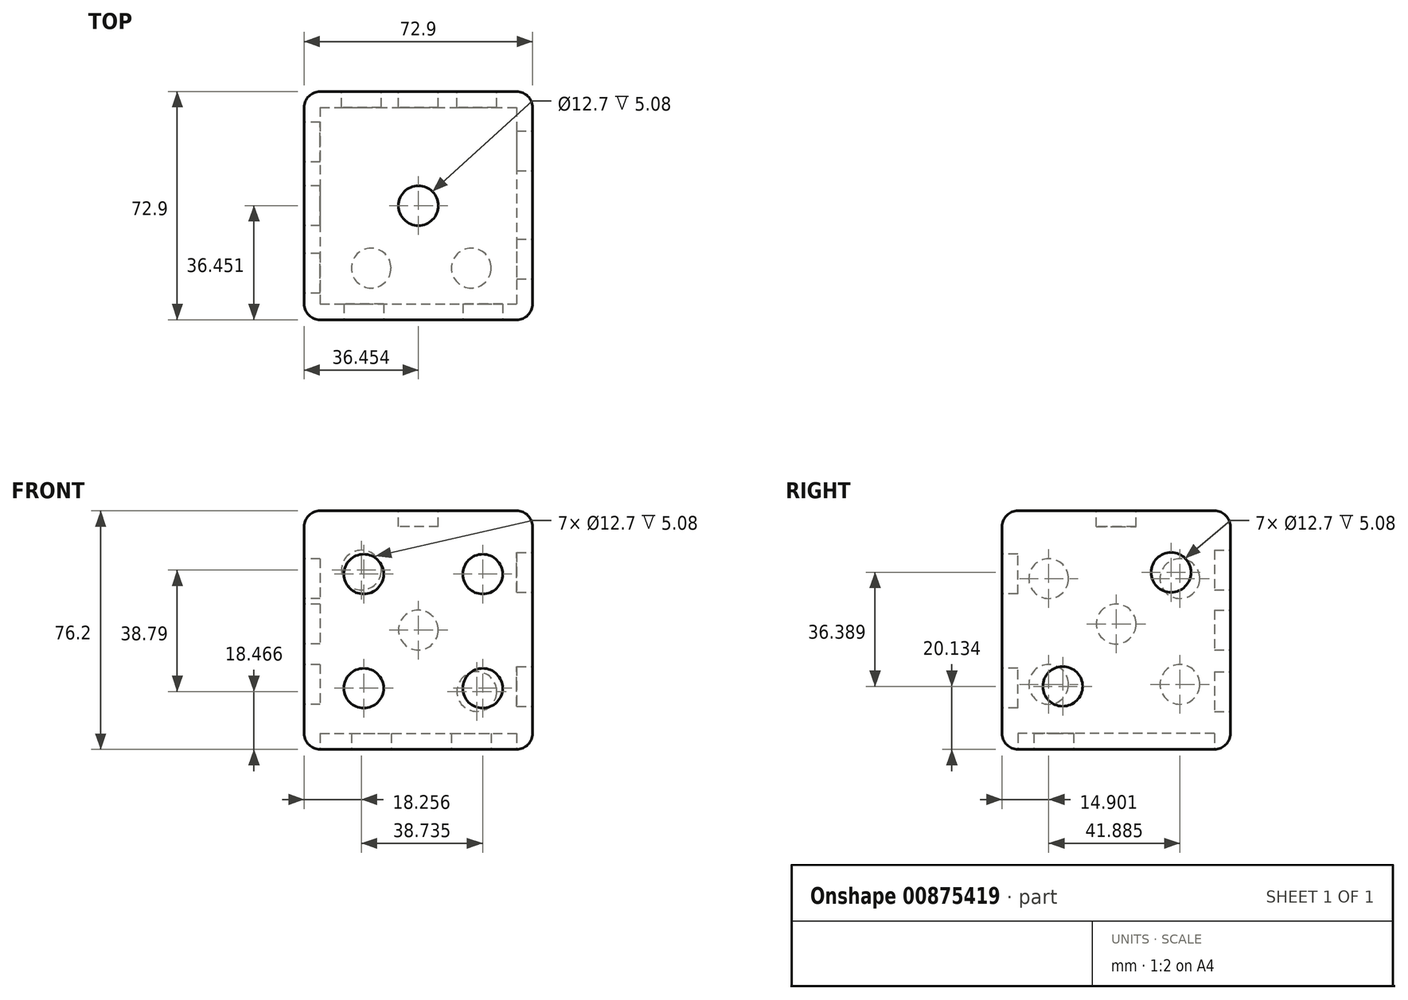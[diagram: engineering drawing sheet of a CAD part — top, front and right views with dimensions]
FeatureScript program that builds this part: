
annotation { "Feature Type Name" : "Feature", "Feature Type Description" : "" }
export const myFeature = defineFeature(function(context is Context, id is Id, definition is map)
    precondition{}
    {
        {
            var Q0;
            Q0=qCreatedBy(makeId("Top.planeOp"),FACE);
            var sketch = newSketch(context, id + "F0", { "sketchPlane" : qUnion([Q0])});
            skLineSegment(sketch, "E0.bottom", {"start": v(-93.39, 58.05) * mm, "end": v(-20.49, 58.05) * mm});
            skLineSegment(sketch, "E0.top", {"start": v(-93.39, -14.85) * mm, "end": v(-20.49, -14.85) * mm});
            skLineSegment(sketch, "E0.left", {"start": v(-93.39, 58.05) * mm, "end": v(-93.39, -14.85) * mm});
            skLineSegment(sketch, "E0.right", {"start": v(-20.49, 58.05) * mm, "end": v(-20.49, -14.85) * mm});
            skSolve(sketch);
        }
        {
            var Q0;
            Q0=makeQuery(id+"F0.imprint","IMPRINT",FACE,{"disambiguationData":[TD([[makeQuery(id+"F0.imprint","IMPRINT",EDGE,{"derivedFrom":sQuery(id+"F0.wireOp",EDGE,"E0.bottom")}),-1.0]])]});
            extrude(context, id + "F1", {"entities" : qUnion([Q0]), "depth" : 76.2 * mm, "offsetDistance" : 25.4 * mm});
        }
        {
            var Q0;
            Q0=makeQuery(id+"F1.opExtrude","CAP_EDGE",EDGE,{"disambiguationData":[OSD([sQuery(id+"F0.wireOp",EDGE,"E0.right")])],"isStart":false});
            var Q1;
            Q1=makeQuery(id+"F1.opExtrude","SWEPT_EDGE",EDGE,{"disambiguationData":[OSD([sQuery(id+"F0.wireOp",EDGE,"E0.bottom"),sQuery(id+"F0.wireOp",EDGE,"E0.left")])]});
            var Q2;
            Q2=makeQuery(id+"F1.opExtrude","CAP_EDGE",EDGE,{"disambiguationData":[OSD([sQuery(id+"F0.wireOp",EDGE,"E0.bottom")])],"isStart":true});
            var Q3;
            Q3=makeQuery(id+"F1.opExtrude","SWEPT_EDGE",EDGE,{"disambiguationData":[OSD([sQuery(id+"F0.wireOp",EDGE,"E0.bottom"),sQuery(id+"F0.wireOp",EDGE,"E0.right")])]});
            var Q4;
            Q4=makeQuery(id+"F1.opExtrude","CAP_EDGE",EDGE,{"disambiguationData":[OSD([sQuery(id+"F0.wireOp",EDGE,"E0.right")])],"isStart":true});
            var Q5;
            Q5=makeQuery(id+"F1.opExtrude","CAP_EDGE",EDGE,{"disambiguationData":[OSD([sQuery(id+"F0.wireOp",EDGE,"E0.bottom")])],"isStart":false});
            var Q6;
            Q6=makeQuery(id+"F1.opExtrude","SWEPT_EDGE",EDGE,{"disambiguationData":[OSD([sQuery(id+"F0.wireOp",EDGE,"E0.top"),sQuery(id+"F0.wireOp",EDGE,"E0.right")])]});
            var Q7;
            Q7=makeQuery(id+"F1.opExtrude","CAP_EDGE",EDGE,{"disambiguationData":[OSD([sQuery(id+"F0.wireOp",EDGE,"E0.left")])],"isStart":true});
            var Q8;
            Q8=makeQuery(id+"F1.opExtrude","CAP_EDGE",EDGE,{"disambiguationData":[OSD([sQuery(id+"F0.wireOp",EDGE,"E0.top")])],"isStart":true});
            var Q9;
            Q9=makeQuery(id+"F1.opExtrude","CAP_EDGE",EDGE,{"disambiguationData":[OSD([sQuery(id+"F0.wireOp",EDGE,"E0.top")])],"isStart":false});
            var Q10;
            Q10=makeQuery(id+"F1.opExtrude","SWEPT_EDGE",EDGE,{"disambiguationData":[OSD([sQuery(id+"F0.wireOp",EDGE,"E0.top"),sQuery(id+"F0.wireOp",EDGE,"E0.left")])]});
            var Q11;
            Q11=makeQuery(id+"F1.opExtrude","CAP_EDGE",EDGE,{"disambiguationData":[OSD([sQuery(id+"F0.wireOp",EDGE,"E0.left")])],"isStart":false});
            fillet(context, id + "F2", {"entities" : qUnion([Q0, Q1, Q2, Q3, Q4, Q5, Q6, Q7, Q8, Q9, Q10, Q11]), "radius" : 5.08 * mm, "tangentPropagation" : true, "allowEdgeOverflow" : false});
        }
        {
            var Q0;
            Q0=makeQuery(id+"F1.opExtrude","CAP_FACE",FACE,{"disambiguationData":[OSD([sQuery(id+"F0.wireOp",EDGE,"E0.bottom"),sQuery(id+"F0.wireOp",EDGE,"E0.top"),sQuery(id+"F0.wireOp",EDGE,"E0.left"),sQuery(id+"F0.wireOp",EDGE,"E0.right")])],"isStart":false});
            var sketch = newSketch(context, id + "F3", { "sketchPlane" : qUnion([Q0])});
            skLineSegment(sketch, "E1.0.0", {"start": v(-88.3, -9.77) * mm, "end": v(-25.57, -9.77) * mm});
            skLineSegment(sketch, "E1.0.1", {"start": v(-25.57, -9.77) * mm, "end": v(-25.57, 52.97) * mm});
            skLineSegment(sketch, "E1.0.2", {"start": v(-25.57, 52.97) * mm, "end": v(-88.3, 52.97) * mm});
            skLineSegment(sketch, "E1.0.3", {"start": v(-88.3, 52.97) * mm, "end": v(-88.3, -9.77) * mm});
            skLineSegment(sketch, "E2", {"start": v(-56.94, 52.97) * mm, "end": v(-56.94, -9.77) * mm, "construction": true});
            skLineSegment(sketch, "E3", {"start": v(-88.3, 21.6) * mm, "end": v(-25.57, 21.6) * mm, "construction": true});
            skCircle(sketch, "E4", {"center": v(-56.94, 21.6) * mm, "radius": 6.35 * mm});
            skSolve(sketch);
        }
        {
            var Q0;
            Q0=makeQuery(id+"F3.imprint","IMPRINT",FACE,{"disambiguationData":[TD([[makeQuery(id+"F3.imprint","IMPRINT",EDGE,{"derivedFrom":sQuery(id+"F3.wireOp",EDGE,"E4")}),1.0]])]});
            extrude(context, id + "F4", {"entities" : qUnion([Q0]), "operationType" : NewBodyOperationType.REMOVE, "oppositeDirection" : true, "depth" : 5.08 * mm, "offsetDistance" : 25.4 * mm});
        }
        {
            var Q0;
            Q0=makeQuery(id+"F1.opExtrude","CAP_FACE",FACE,{"disambiguationData":[OSD([sQuery(id+"F0.wireOp",EDGE,"E0.bottom"),sQuery(id+"F0.wireOp",EDGE,"E0.top"),sQuery(id+"F0.wireOp",EDGE,"E0.left"),sQuery(id+"F0.wireOp",EDGE,"E0.right")])],"isStart":true});
            var sketch = newSketch(context, id + "F5", { "sketchPlane" : qUnion([Q0])});
            skLineSegment(sketch, "E5.0.0", {"start": v(-88.3, -52.97) * mm, "end": v(-25.57, -52.97) * mm});
            skLineSegment(sketch, "E5.0.1", {"start": v(-25.57, -52.97) * mm, "end": v(-25.57, 9.77) * mm});
            skLineSegment(sketch, "E5.0.2", {"start": v(-25.57, 9.77) * mm, "end": v(-88.3, 9.77) * mm});
            skLineSegment(sketch, "E5.0.3", {"start": v(-88.3, 9.77) * mm, "end": v(-88.3, -52.97) * mm});
            skLineSegment(sketch, "E6", {"start": v(-72, 9.77) * mm, "end": v(-72, -52.97) * mm});
            skLineSegment(sketch, "E7", {"start": v(-40.03, 9.77) * mm, "end": v(-40.03, -52.97) * mm});
            skCircle(sketch, "E8", {"center": v(-72, -1.66) * mm, "radius": 6.35 * mm});
            skCircle(sketch, "E9", {"center": v(-72, -21.6) * mm, "radius": 6.35 * mm});
            skCircle(sketch, "E10", {"center": v(-72, -41.54) * mm, "radius": 6.35 * mm});
            skCircle(sketch, "E11", {"center": v(-40.03, -1.66) * mm, "radius": 6.35 * mm});
            skCircle(sketch, "E12", {"center": v(-40.03, -21.6) * mm, "radius": 6.35 * mm});
            skCircle(sketch, "E13", {"center": v(-40.03, -41.54) * mm, "radius": 6.35 * mm});
            skSolve(sketch);
        }
        {
            var Q0;
            {var subQ0=sQuery(id+"F5.wireOp",EDGE,"E8");var subQ1=sQuery(id+"F5.wireOp",EDGE,"E6");var subQ2=makeQuery(id+"F5.imprint","INTERSECT",VERTEX,{"disambiguationData":[OD(0.0)],"derivedFrom":[subQ1,subQ0]});Q0=makeQuery(id+"F5.imprint","IMPRINT",FACE,{"disambiguationData":[TD([[makeQuery(id+"F5.imprint","IMPRINT",EDGE,{"disambiguationData":[TD([[subQ2,-1.0]])],"derivedFrom":subQ1}),-1.0]])]});}
            var Q1;
            {var subQ0=sQuery(id+"F5.wireOp",EDGE,"E8");var subQ1=sQuery(id+"F5.wireOp",EDGE,"E6");var subQ2=makeQuery(id+"F5.imprint","INTERSECT",VERTEX,{"disambiguationData":[OD(0.0)],"derivedFrom":[subQ1,subQ0]});Q1=makeQuery(id+"F5.imprint","IMPRINT",FACE,{"disambiguationData":[TD([[makeQuery(id+"F5.imprint","IMPRINT",EDGE,{"disambiguationData":[TD([[subQ2,-1.0]])],"derivedFrom":subQ1}),1.0]])]});}
            var Q2;
            {var subQ0=sQuery(id+"F5.wireOp",EDGE,"E9");var subQ1=sQuery(id+"F5.wireOp",EDGE,"E6");var subQ2=makeQuery(id+"F5.imprint","INTERSECT",VERTEX,{"disambiguationData":[OD(0.0)],"derivedFrom":[subQ1,subQ0]});Q2=makeQuery(id+"F5.imprint","IMPRINT",FACE,{"disambiguationData":[TD([[makeQuery(id+"F5.imprint","IMPRINT",EDGE,{"disambiguationData":[TD([[subQ2,-1.0]])],"derivedFrom":subQ1}),-1.0]])]});}
            var Q3;
            {var subQ0=sQuery(id+"F5.wireOp",EDGE,"E9");var subQ1=sQuery(id+"F5.wireOp",EDGE,"E6");var subQ2=makeQuery(id+"F5.imprint","INTERSECT",VERTEX,{"disambiguationData":[OD(0.0)],"derivedFrom":[subQ1,subQ0]});Q3=makeQuery(id+"F5.imprint","IMPRINT",FACE,{"disambiguationData":[TD([[makeQuery(id+"F5.imprint","IMPRINT",EDGE,{"disambiguationData":[TD([[subQ2,-1.0]])],"derivedFrom":subQ1}),1.0]])]});}
            var Q4;
            {var subQ0=sQuery(id+"F5.wireOp",EDGE,"E10");var subQ1=sQuery(id+"F5.wireOp",EDGE,"E6");var subQ2=makeQuery(id+"F5.imprint","INTERSECT",VERTEX,{"disambiguationData":[OD(0.0)],"derivedFrom":[subQ1,subQ0]});Q4=makeQuery(id+"F5.imprint","IMPRINT",FACE,{"disambiguationData":[TD([[makeQuery(id+"F5.imprint","IMPRINT",EDGE,{"disambiguationData":[TD([[subQ2,-1.0]])],"derivedFrom":subQ1}),-1.0]])]});}
            var Q5;
            {var subQ0=sQuery(id+"F5.wireOp",EDGE,"E13");var subQ1=sQuery(id+"F5.wireOp",EDGE,"E7");var subQ2=makeQuery(id+"F5.imprint","INTERSECT",VERTEX,{"disambiguationData":[OD(0.0)],"derivedFrom":[subQ1,subQ0]});Q5=makeQuery(id+"F5.imprint","IMPRINT",FACE,{"disambiguationData":[TD([[makeQuery(id+"F5.imprint","IMPRINT",EDGE,{"disambiguationData":[TD([[subQ2,-1.0]])],"derivedFrom":subQ1}),-1.0]])]});}
            var Q6;
            {var subQ0=sQuery(id+"F5.wireOp",EDGE,"E13");var subQ1=sQuery(id+"F5.wireOp",EDGE,"E7");var subQ2=makeQuery(id+"F5.imprint","INTERSECT",VERTEX,{"disambiguationData":[OD(0.0)],"derivedFrom":[subQ1,subQ0]});Q6=makeQuery(id+"F5.imprint","IMPRINT",FACE,{"disambiguationData":[TD([[makeQuery(id+"F5.imprint","IMPRINT",EDGE,{"disambiguationData":[TD([[subQ2,-1.0]])],"derivedFrom":subQ1}),1.0]])]});}
            var Q7;
            {var subQ0=sQuery(id+"F5.wireOp",EDGE,"E12");var subQ1=sQuery(id+"F5.wireOp",EDGE,"E7");var subQ2=makeQuery(id+"F5.imprint","INTERSECT",VERTEX,{"disambiguationData":[OD(0.0)],"derivedFrom":[subQ1,subQ0]});Q7=makeQuery(id+"F5.imprint","IMPRINT",FACE,{"disambiguationData":[TD([[makeQuery(id+"F5.imprint","IMPRINT",EDGE,{"disambiguationData":[TD([[subQ2,-1.0]])],"derivedFrom":subQ1}),-1.0]])]});}
            var Q8;
            {var subQ0=sQuery(id+"F5.wireOp",EDGE,"E12");var subQ1=sQuery(id+"F5.wireOp",EDGE,"E7");var subQ2=makeQuery(id+"F5.imprint","INTERSECT",VERTEX,{"disambiguationData":[OD(0.0)],"derivedFrom":[subQ1,subQ0]});Q8=makeQuery(id+"F5.imprint","IMPRINT",FACE,{"disambiguationData":[TD([[makeQuery(id+"F5.imprint","IMPRINT",EDGE,{"disambiguationData":[TD([[subQ2,-1.0]])],"derivedFrom":subQ1}),1.0]])]});}
            var Q9;
            {var subQ0=sQuery(id+"F5.wireOp",EDGE,"E11");var subQ1=sQuery(id+"F5.wireOp",EDGE,"E7");var subQ2=makeQuery(id+"F5.imprint","INTERSECT",VERTEX,{"disambiguationData":[OD(0.0)],"derivedFrom":[subQ1,subQ0]});Q9=makeQuery(id+"F5.imprint","IMPRINT",FACE,{"disambiguationData":[TD([[makeQuery(id+"F5.imprint","IMPRINT",EDGE,{"disambiguationData":[TD([[subQ2,-1.0]])],"derivedFrom":subQ1}),-1.0]])]});}
            var Q10;
            {var subQ0=sQuery(id+"F5.wireOp",EDGE,"E11");var subQ1=sQuery(id+"F5.wireOp",EDGE,"E7");var subQ2=makeQuery(id+"F5.imprint","INTERSECT",VERTEX,{"disambiguationData":[OD(0.0)],"derivedFrom":[subQ1,subQ0]});Q10=makeQuery(id+"F5.imprint","IMPRINT",FACE,{"disambiguationData":[TD([[makeQuery(id+"F5.imprint","IMPRINT",EDGE,{"disambiguationData":[TD([[subQ2,-1.0]])],"derivedFrom":subQ1}),1.0]])]});}
            var Q11;
            {var subQ0=sQuery(id+"F5.wireOp",EDGE,"E10");var subQ1=sQuery(id+"F5.wireOp",EDGE,"E6");var subQ2=makeQuery(id+"F5.imprint","INTERSECT",VERTEX,{"disambiguationData":[OD(0.0)],"derivedFrom":[subQ1,subQ0]});Q11=makeQuery(id+"F5.imprint","IMPRINT",FACE,{"disambiguationData":[TD([[makeQuery(id+"F5.imprint","IMPRINT",EDGE,{"disambiguationData":[TD([[subQ2,-1.0]])],"derivedFrom":subQ1}),1.0]])]});}
            extrude(context, id + "F6", {"entities" : qUnion([Q0, Q1, Q2, Q3, Q4, Q5, Q6, Q7, Q8, Q9, Q10, Q11]), "operationType" : NewBodyOperationType.REMOVE, "oppositeDirection" : true, "depth" : 5.08 * mm, "offsetDistance" : 25.4 * mm});
        }
        {
            var Q0;
            Q0=makeQuery(id+"F1.opExtrude","SWEPT_FACE",FACE,{"disambiguationData":[OSD([sQuery(id+"F0.wireOp",EDGE,"E0.right")])]});
            var sketch = newSketch(context, id + "F7", { "sketchPlane" : qUnion([Q0])});
            skLineSegment(sketch, "E14", {"start": v(52.97, 71.12) * mm, "end": v(-9.77, 5.08) * mm, "construction": true});
            skCircle(sketch, "E15", {"center": v(39.1, 56.52) * mm, "radius": 6.35 * mm});
            skCircle(sketch, "E16", {"center": v(4.53, 20.13) * mm, "radius": 6.35 * mm});
            skSolve(sketch);
        }
        {
            var Q0;
            Q0=makeQuery(id+"F7.imprint","IMPRINT",FACE,{"disambiguationData":[TD([[makeQuery(id+"F7.imprint","IMPRINT",EDGE,{"derivedFrom":sQuery(id+"F7.wireOp",EDGE,"E15")}),1.0]])]});
            var Q1;
            Q1=makeQuery(id+"F7.imprint","IMPRINT",FACE,{"disambiguationData":[TD([[makeQuery(id+"F7.imprint","IMPRINT",EDGE,{"derivedFrom":sQuery(id+"F7.wireOp",EDGE,"E16")}),1.0]])]});
            extrude(context, id + "F8", {"entities" : qUnion([Q0, Q1]), "operationType" : NewBodyOperationType.REMOVE, "oppositeDirection" : true, "depth" : 5.08 * mm, "offsetDistance" : 25.4 * mm});
        }
        {
            var Q0;
            Q0=makeQuery(id+"F1.opExtrude","SWEPT_FACE",FACE,{"disambiguationData":[OSD([sQuery(id+"F0.wireOp",EDGE,"E0.bottom")])]});
            var sketch = newSketch(context, id + "F9", { "sketchPlane" : qUnion([Q0])});
            skLineSegment(sketch, "E17", {"start": v(25.57, 5.08) * mm, "end": v(88.3, 71.12) * mm, "construction": true});
            skCircle(sketch, "E18", {"center": v(56.94, 38.1) * mm, "radius": 6.35 * mm});
            skCircle(sketch, "E19", {"center": v(38.28, 18.47) * mm, "radius": 6.35 * mm});
            skCircle(sketch, "E20", {"center": v(75.13, 57.26) * mm, "radius": 6.35 * mm});
            skSolve(sketch);
        }
        {
            var Q0;
            Q0=makeQuery(id+"F9.imprint","IMPRINT",FACE,{"disambiguationData":[TD([[makeQuery(id+"F9.imprint","IMPRINT",EDGE,{"derivedFrom":sQuery(id+"F9.wireOp",EDGE,"E20")}),1.0]])]});
            var Q1;
            Q1=makeQuery(id+"F9.imprint","IMPRINT",FACE,{"disambiguationData":[TD([[makeQuery(id+"F9.imprint","IMPRINT",EDGE,{"derivedFrom":sQuery(id+"F9.wireOp",EDGE,"E18")}),1.0]])]});
            var Q2;
            Q2=makeQuery(id+"F9.imprint","IMPRINT",FACE,{"disambiguationData":[TD([[makeQuery(id+"F9.imprint","IMPRINT",EDGE,{"derivedFrom":sQuery(id+"F9.wireOp",EDGE,"E19")}),1.0]])]});
            extrude(context, id + "F10", {"entities" : qUnion([Q0, Q1, Q2]), "operationType" : NewBodyOperationType.REMOVE, "oppositeDirection" : true, "depth" : 5.08 * mm, "offsetDistance" : 25.4 * mm});
        }
        {
            var Q0;
            Q0=makeQuery(id+"F1.opExtrude","SWEPT_FACE",FACE,{"disambiguationData":[OSD([sQuery(id+"F0.wireOp",EDGE,"E0.top")])]});
            var sketch = newSketch(context, id + "F11", { "sketchPlane" : qUnion([Q0])});
            skLineSegment(sketch, "E21", {"start": v(-74.36, 71.12) * mm, "end": v(-74.36, 5.08) * mm, "construction": true});
            skLineSegment(sketch, "E22", {"start": v(-36.4, 71.12) * mm, "end": v(-36.4, 5.08) * mm, "construction": true});
            skCircle(sketch, "E23", {"center": v(-74.36, 55.97) * mm, "radius": 6.35 * mm});
            skCircle(sketch, "E24", {"center": v(-74.36, 19.52) * mm, "radius": 6.35 * mm});
            skCircle(sketch, "E25", {"center": v(-36.4, 55.97) * mm, "radius": 6.35 * mm});
            skCircle(sketch, "E26", {"center": v(-36.4, 19.52) * mm, "radius": 6.35 * mm});
            skSolve(sketch);
        }
        {
            var Q0;
            Q0=makeQuery(id+"F11.imprint","IMPRINT",FACE,{"disambiguationData":[TD([[makeQuery(id+"F11.imprint","IMPRINT",EDGE,{"derivedFrom":sQuery(id+"F11.wireOp",EDGE,"E23")}),1.0]])]});
            var Q1;
            Q1=makeQuery(id+"F11.imprint","IMPRINT",FACE,{"disambiguationData":[TD([[makeQuery(id+"F11.imprint","IMPRINT",EDGE,{"derivedFrom":sQuery(id+"F11.wireOp",EDGE,"E25")}),1.0]])]});
            var Q2;
            Q2=makeQuery(id+"F11.imprint","IMPRINT",FACE,{"disambiguationData":[TD([[makeQuery(id+"F11.imprint","IMPRINT",EDGE,{"derivedFrom":sQuery(id+"F11.wireOp",EDGE,"E26")}),1.0]])]});
            var Q3;
            Q3=makeQuery(id+"F11.imprint","IMPRINT",FACE,{"disambiguationData":[TD([[makeQuery(id+"F11.imprint","IMPRINT",EDGE,{"derivedFrom":sQuery(id+"F11.wireOp",EDGE,"E24")}),1.0]])]});
            extrude(context, id + "F12", {"entities" : qUnion([Q0, Q1, Q2, Q3]), "operationType" : NewBodyOperationType.REMOVE, "oppositeDirection" : true, "depth" : 5.08 * mm, "offsetDistance" : 25.4 * mm});
        }
        {
            var Q0;
            Q0=makeQuery(id+"F1.opExtrude","SWEPT_FACE",FACE,{"disambiguationData":[OSD([sQuery(id+"F0.wireOp",EDGE,"E0.left")])]});
            var sketch = newSketch(context, id + "F13", { "sketchPlane" : qUnion([Q0])});
            skLineSegment(sketch, "E27", {"start": v(-21.6, 71.12) * mm, "end": v(-21.6, 5.08) * mm, "construction": true});
            skCircle(sketch, "E28", {"center": v(-21.6, 40.04) * mm, "radius": 6.35 * mm});
            skLineSegment(sketch, "E29", {"start": v(-41.94, 71.12) * mm, "end": v(-41.94, 5.08) * mm, "construction": true});
            skLineSegment(sketch, "E30", {"start": v(-0.05, 71.12) * mm, "end": v(-0.05, 5.08) * mm, "construction": true});
            skCircle(sketch, "E31", {"center": v(-41.94, 54.54) * mm, "radius": 6.35 * mm});
            skCircle(sketch, "E32", {"center": v(-41.94, 20.76) * mm, "radius": 6.35 * mm});
            skCircle(sketch, "E33", {"center": v(-0.05, 54.54) * mm, "radius": 6.35 * mm});
            skCircle(sketch, "E34", {"center": v(-0.05, 20.76) * mm, "radius": 6.35 * mm});
            skSolve(sketch);
        }
        {
            var Q0;
            Q0=makeQuery(id+"F13.imprint","IMPRINT",FACE,{"disambiguationData":[TD([[makeQuery(id+"F13.imprint","IMPRINT",EDGE,{"derivedFrom":sQuery(id+"F13.wireOp",EDGE,"E31")}),1.0]])]});
            var Q1;
            Q1=makeQuery(id+"F13.imprint","IMPRINT",FACE,{"disambiguationData":[TD([[makeQuery(id+"F13.imprint","IMPRINT",EDGE,{"derivedFrom":sQuery(id+"F13.wireOp",EDGE,"E28")}),1.0]])]});
            var Q2;
            Q2=makeQuery(id+"F13.imprint","IMPRINT",FACE,{"disambiguationData":[TD([[makeQuery(id+"F13.imprint","IMPRINT",EDGE,{"derivedFrom":sQuery(id+"F13.wireOp",EDGE,"E33")}),1.0]])]});
            var Q3;
            Q3=makeQuery(id+"F13.imprint","IMPRINT",FACE,{"disambiguationData":[TD([[makeQuery(id+"F13.imprint","IMPRINT",EDGE,{"derivedFrom":sQuery(id+"F13.wireOp",EDGE,"E34")}),1.0]])]});
            var Q4;
            Q4=makeQuery(id+"F13.imprint","IMPRINT",FACE,{"disambiguationData":[TD([[makeQuery(id+"F13.imprint","IMPRINT",EDGE,{"derivedFrom":sQuery(id+"F13.wireOp",EDGE,"E32")}),1.0]])]});
            extrude(context, id + "F14", {"entities" : qUnion([Q0, Q1, Q2, Q3, Q4]), "operationType" : NewBodyOperationType.REMOVE, "oppositeDirection" : true, "depth" : 5.08 * mm, "offsetDistance" : 25.4 * mm});
        }
    });
